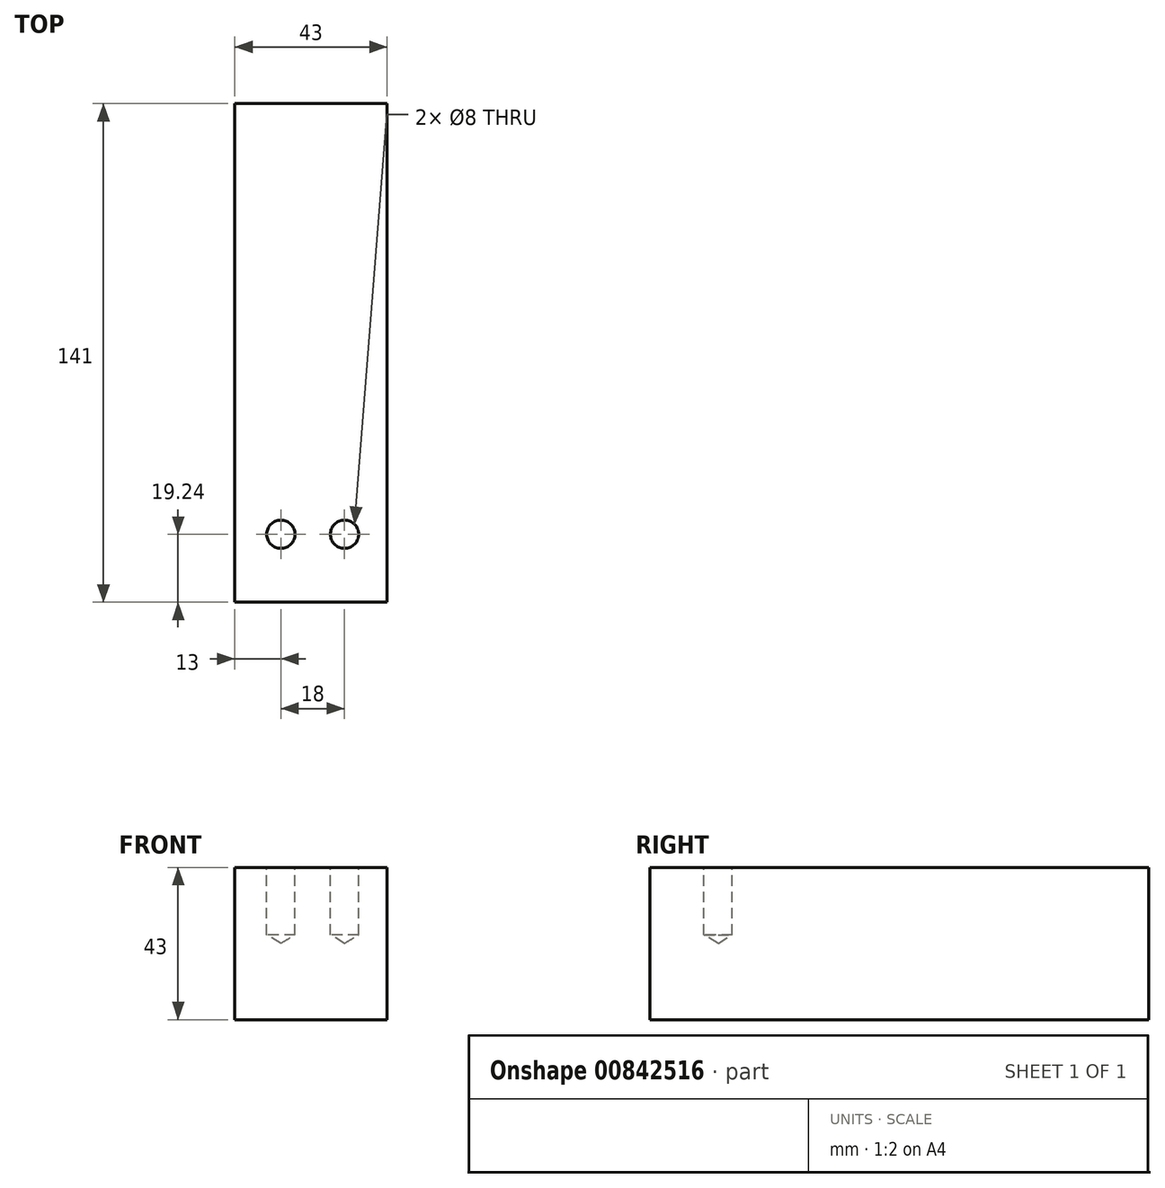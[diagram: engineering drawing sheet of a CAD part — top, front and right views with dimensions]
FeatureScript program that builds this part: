
annotation { "Feature Type Name" : "Feature", "Feature Type Description" : "" }
export const myFeature = defineFeature(function(context is Context, id is Id, definition is map)
    precondition{}
    {
        {
            var Q0;
            Q0=qCreatedBy(makeId("Front.planeOp"),FACE);
            var sketch = newSketch(context, id + "F0", { "sketchPlane" : qUnion([Q0])});
            skLineSegment(sketch, "E0.bottom", {"start": v(0, 0) * mm, "end": v(43, 0) * mm});
            skLineSegment(sketch, "E0.top", {"start": v(0, 43) * mm, "end": v(43, 43) * mm});
            skLineSegment(sketch, "E0.left", {"start": v(0, 0) * mm, "end": v(0, 43) * mm});
            skLineSegment(sketch, "E0.right", {"start": v(43, 0) * mm, "end": v(43, 43) * mm});
            skSolve(sketch);
        }
        {
            var Q0;
            Q0 = qSketchRegion(id + "F0", true);
            var Q1;
            Q1=makeQuery(id+"F0.imprint","IMPRINT",FACE,{"disambiguationData":[TD([[makeQuery(id+"F0.imprint","IMPRINT",EDGE,{"derivedFrom":sQuery(id+"F0.wireOp",EDGE,"E0.bottom")}),1.0]])]});
            extrude(context, id + "F1", {"entities" : qUnion([Q0, Q1]), "depth" : 141 * mm, "offsetDistance" : 25 * mm});
        }
        {
            var Q0;
            Q0=makeQuery(id+"F1.opExtrude","SWEPT_FACE",FACE,{"disambiguationData":[OSD([sQuery(id+"F0.wireOp",EDGE,"E0.top")])]});
            var sketch = newSketch(context, id + "F2", { "sketchPlane" : qUnion([Q0])});
            skLineSegment(sketch, "E1", {"start": v(0, -111.71) * mm, "end": v(9, -111.71) * mm});
            skLineSegment(sketch, "E2", {"start": v(9, -111.71) * mm, "end": v(9, 0) * mm});
            skLineSegment(sketch, "E3", {"start": v(9, 0) * mm, "end": v(9, -141) * mm});
            skLineSegment(sketch, "E4", {"start": v(43, -141) * mm, "end": v(35, -141) * mm});
            skLineSegment(sketch, "E5", {"start": v(9, -141) * mm, "end": v(9, -121.76) * mm});
            skLineSegment(sketch, "E6", {"start": v(9, -121.76) * mm, "end": v(13, -121.76) * mm});
            skCircle(sketch, "E7", {"center": v(13, -121.76) * mm, "radius": 4 * mm});
            skLineSegment(sketch, "E8", {"start": v(35, -141) * mm, "end": v(35, 0) * mm});
            skLineSegment(sketch, "E9", {"start": v(35, -121.76) * mm, "end": v(31, -121.76) * mm});
            skCircle(sketch, "E10", {"center": v(31, -121.76) * mm, "radius": 4 * mm});
            skSolve(sketch);
        }
        {
            var Q0;
            Q0=sQuery(id+"F2.wireOp",VERTEX,"E9.end");
            var Q1;
            Q1=makeQuery(id+"F1.opExtrude","SWEPT_BODY",BODY,{"disambiguationData":[OSD([sQuery(id+"F0.wireOp",EDGE,"E0.bottom"),sQuery(id+"F0.wireOp",EDGE,"E0.top"),sQuery(id+"F0.wireOp",EDGE,"E0.left"),sQuery(id+"F0.wireOp",EDGE,"E0.right")])]});
            hole(context, id + "F3", {"style" : HoleStyle.SIMPLE, "endStyle" : HoleEndStyle.BLIND, "holeDiameter" : 8 * mm, "majorDiameter" : 5 * mm, "holeDepth" : 19 * mm, "isTappedThrough" : true, "tappedDepth" : 12 * mm, "tapClearance" : 3, "locations" : qUnion([Q0]), "scope" : qUnion([Q1])});
        }
        {
            var Q0;
            Q0=sQuery(id+"F2.wireOp",VERTEX,"E6.end");
            var Q1;
            Q1=makeQuery(id+"F1.opExtrude","SWEPT_BODY",BODY,{"disambiguationData":[OSD([sQuery(id+"F0.wireOp",EDGE,"E0.bottom"),sQuery(id+"F0.wireOp",EDGE,"E0.top"),sQuery(id+"F0.wireOp",EDGE,"E0.left"),sQuery(id+"F0.wireOp",EDGE,"E0.right")])]});
            hole(context, id + "F4", {"style" : HoleStyle.SIMPLE, "endStyle" : HoleEndStyle.BLIND, "holeDiameter" : 8 * mm, "majorDiameter" : 5 * mm, "holeDepth" : 19 * mm, "isTappedThrough" : true, "tappedDepth" : 12 * mm, "tapClearance" : 3, "locations" : qUnion([Q0]), "scope" : qUnion([Q1])});
        }
    });
